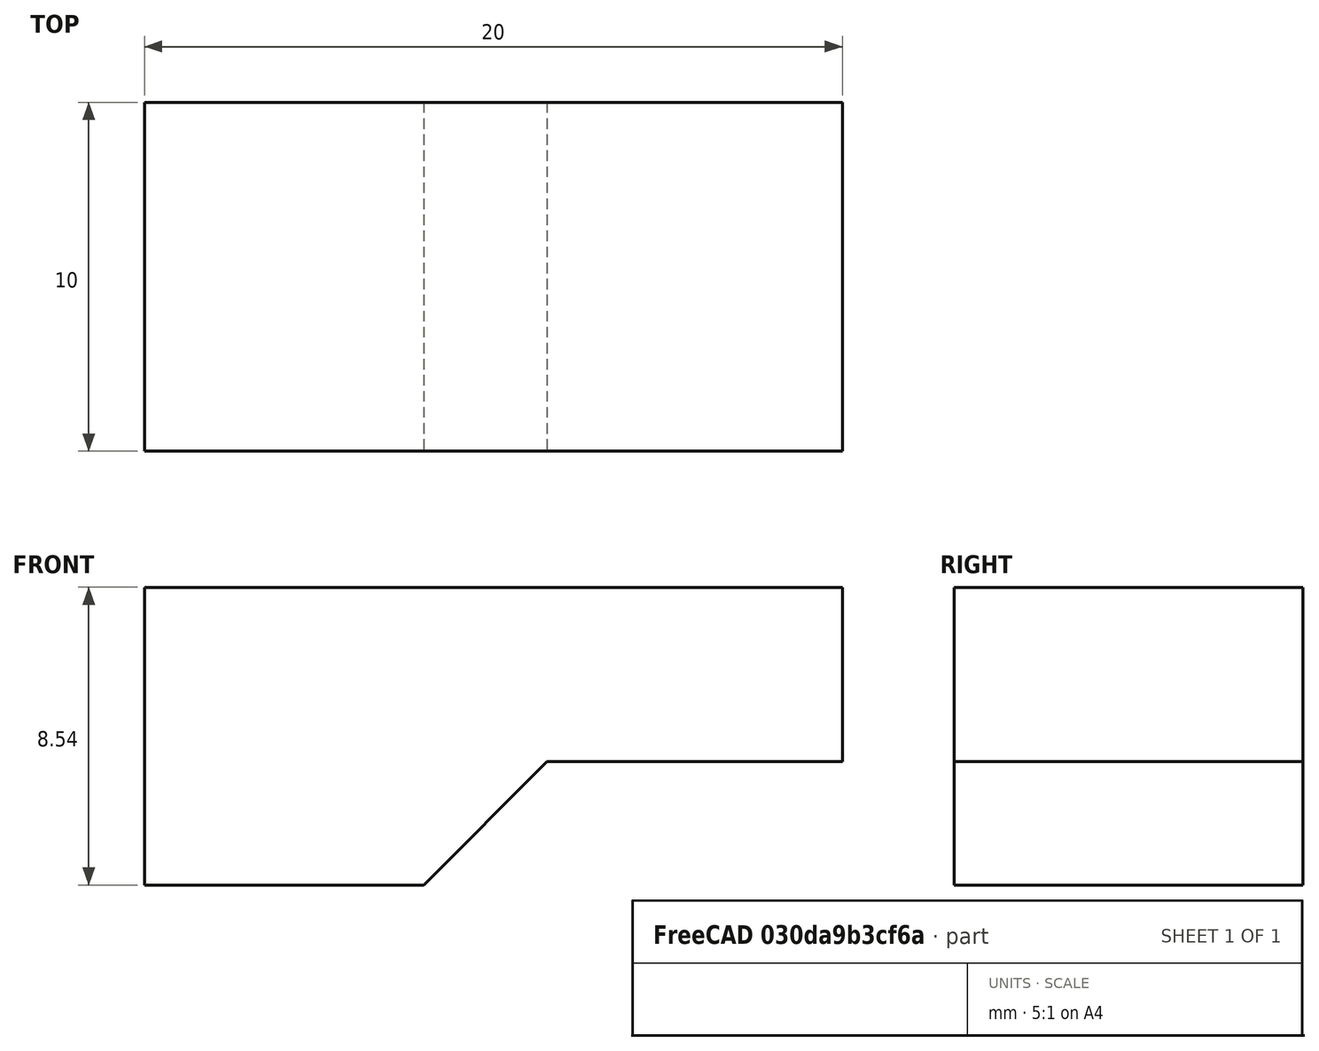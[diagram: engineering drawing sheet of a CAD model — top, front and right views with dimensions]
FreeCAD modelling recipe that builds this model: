
FCSTD DOCUMENT  (FreeCAD 1.0R38641 +468 (Git))
Label: tool_support_test
License: All rights reserved
LicenseURL: https://en.wikipedia.org/wiki/All_rights_reserved
objects: Sketcher::SketchObject×1, PartDesign::Pad×1, PartDesign::Body×1
note: 6 computed .brp shape members not serialized (recipe doc carries the construction recipe); baked Part::Feature solids carry a one-line shape summary decoded from their .brp

FEATURE [Sketcher::SketchObject] Sketch
  ArcFitTolerance = 1e-06
  AttachmentSupport = -> [XY_Plane]
  FullyConstrained = true
  MakeInternals = false
  MapMode = 5
  sketch-geometry (6):
    g0: LineSegment StartX=0 StartY=0 StartZ=0 EndX=8 EndY=0 EndZ=0
    g1: LineSegment StartX=0 StartY=0 StartZ=0 EndX=0 EndY=8.53553 EndZ=0
    g2: LineSegment StartX=0 StartY=8.53553 StartZ=0 EndX=20 EndY=8.53553 EndZ=0
    g3: LineSegment StartX=20 StartY=8.53553 StartZ=0 EndX=20 EndY=3.53553 EndZ=0
    g4: LineSegment StartX=20 StartY=3.53553 StartZ=0 EndX=11.5355 EndY=3.53553 EndZ=0
    g5: LineSegment StartX=11.5355 StartY=3.53553 StartZ=0 EndX=8 EndY=0 EndZ=0
  constraints (17):
    c: Coincident(g0,g-1)
    c: PointOnObject(g0,g-1)
    c: Coincident(g1,g0)
    c: PointOnObject(g1,g-2)
    c: Coincident(g2,g1)
    c: Horizontal(g2)
    c: Coincident(g3,g2)
    c: Vertical(g3)
    c: Coincident(g4,g3)
    c: Horizontal(g4)
    c: Coincident(g5,g4)
    c: Coincident(g5,g0)
    c: Distance(g5,g5) = 5
    c: DistanceY(g3,g3) = 5
    c: Distance(g0,g0) = 8
    c: Distance(g2,g2) = 20
    c: Angle(g5,g-1) = 2.35619
FEATURE [PartDesign::Pad] Pad
  Direction = (0,0,1)
  Length = 10
  Length2 = 10
  Profile = -> Sketch
  ReferenceAxis = -> Sketch [N_Axis]
  Refine = true
  Suppressed = false
  Type = 0
FEATURE [PartDesign::Body] Body  label="tool_support_test"
  AllowCompound = false
  Group = -> [Sketch,Pad]
  Origin = -> Origin
  Placement = pos=(0,0,0) rot=(1,0,0;1.5708rad)
  Tip = -> Pad
